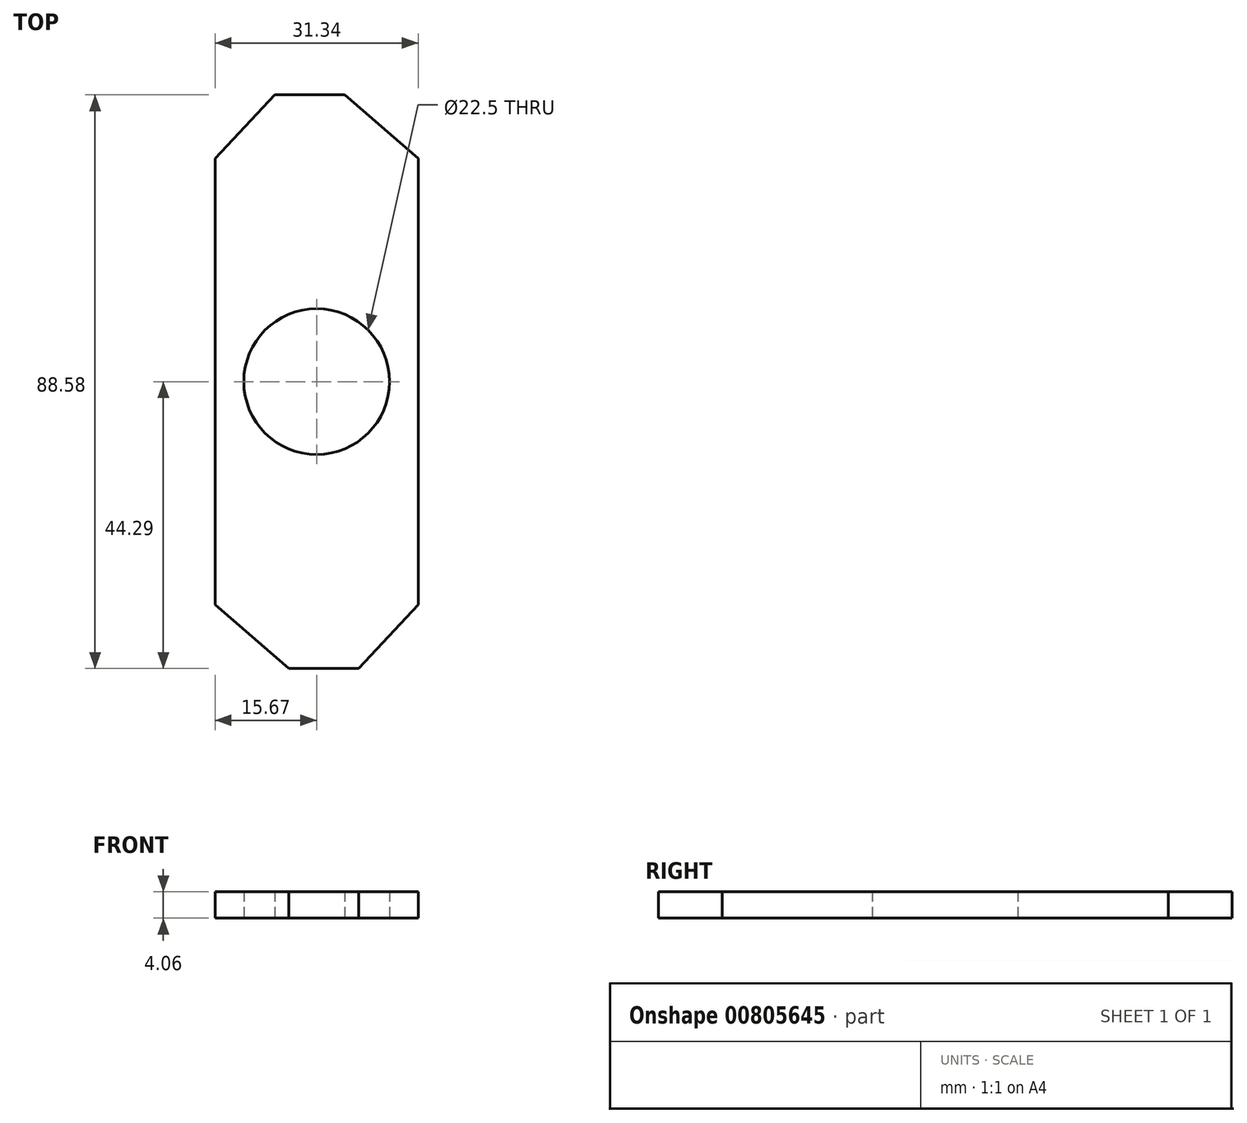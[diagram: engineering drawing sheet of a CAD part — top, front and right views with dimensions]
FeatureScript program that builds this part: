
annotation { "Feature Type Name" : "Feature", "Feature Type Description" : "" }
export const myFeature = defineFeature(function(context is Context, id is Id, definition is map)
    precondition{}
    {
        {
            var Q0;
            Q0=qCreatedBy(makeId("Top.planeOp"),FACE);
            var sketch = newSketch(context, id + "F0", { "sketchPlane" : qUnion([Q0])});
            skCircle(sketch, "E0", {"center": v(0, 0) * mm, "radius": 11.25 * mm});
            skCircle(sketch, "E1", {"center": v(0, 0) * mm, "radius": 15.67 * mm});
            skLineSegment(sketch, "E2", {"start": v(-15.67, 0) * mm, "end": v(-15.67, -34.43) * mm});
            skLineSegment(sketch, "E3", {"start": v(15.67, 0) * mm, "end": v(15.67, -34.43) * mm});
            skLineSegment(sketch, "E4", {"start": v(6.47, -44.29) * mm, "end": v(-4.31, -44.29) * mm});
            skLineSegment(sketch, "E5", {"start": v(15.67, -34.43) * mm, "end": v(6.47, -44.29) * mm});
            skLineSegment(sketch, "E6", {"start": v(-4.31, -44.29) * mm, "end": v(-15.67, -34.43) * mm});
            skPoint(sketch, "E7.orphan", {"position": v(15.67, -44.29) * mm});
            skPoint(sketch, "E8.orphan", {"position": v(-15.67, -44.29) * mm});
            skSolve(sketch);
        }
        {
            var Q0;
            Q0=makeQuery(id+"F0.imprint","IMPRINT",FACE,{"disambiguationData":[TD([[makeQuery(id+"F0.imprint","IMPRINT",EDGE,{"derivedFrom":sQuery(id+"F0.wireOp",EDGE,"E0")}),-1.0]])]});
            var Q1;
            {var subQ0=sQuery(id+"F0.wireOp",EDGE,"E2");Q1=makeQuery(id+"F0.imprint","IMPRINT",FACE,{"disambiguationData":[TD([[makeQuery(id+"F0.imprint","IMPRINT",EDGE,{"derivedFrom":subQ0}),1.0]])]});}
            extrude(context, id + "F1", {"entities" : qUnion([Q0, Q1]), "depth" : 4.06 * mm, "offsetDistance" : 25.4 * mm});
        }
        {
            var Q0;
            Q0=makeQuery(id+"F1.opExtrude","SWEPT_BODY",BODY,{"disambiguationData":[OSD([sQuery(id+"F0.wireOp",EDGE,"E0"),sQuery(id+"F0.wireOp",EDGE,"E1"),sQuery(id+"F0.wireOp",EDGE,"E2"),sQuery(id+"F0.wireOp",EDGE,"E3"),sQuery(id+"F0.wireOp",EDGE,"E4")])]});
            var Q1;
            Q1=makeQuery(id+"F1.opExtrude","CAP_EDGE",EDGE,{"disambiguationData":[OSD([sQuery(id+"F0.wireOp",EDGE,"E0")])],"isStart":false});
            circularPattern(context, id + "F2", {"operationType" : NewBodyOperationType.ADD, "entities" : qUnion([Q0]), "axis" : qUnion([Q1]), "angle" : 360 * degree, "instanceCount" : 2, "equalSpace" : true});
        }
    });
